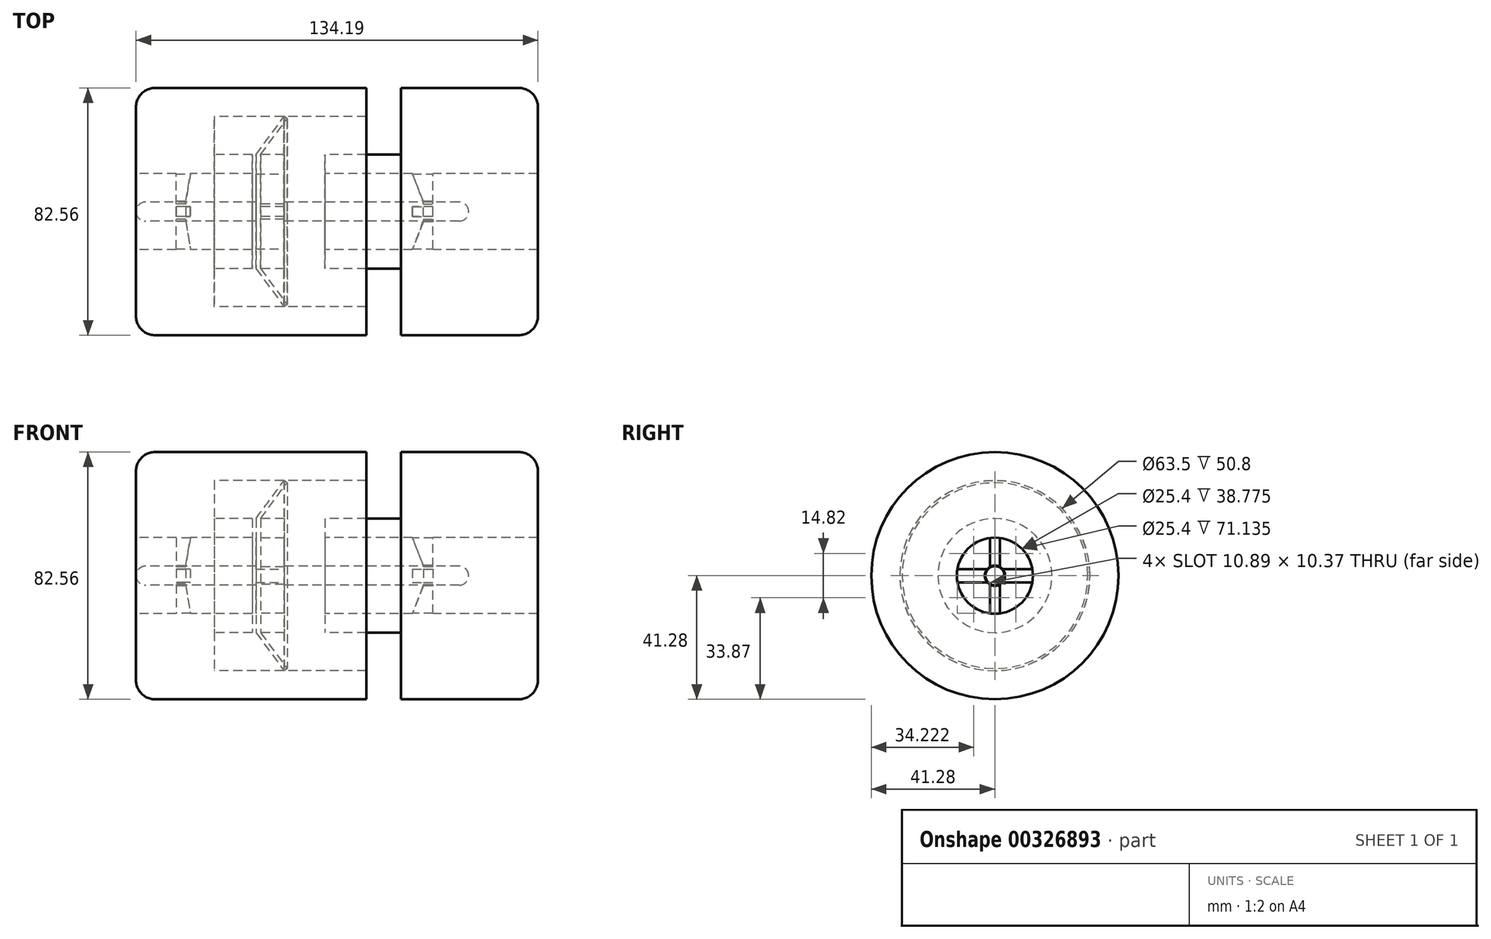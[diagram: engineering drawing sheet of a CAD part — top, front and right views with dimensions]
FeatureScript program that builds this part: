
annotation { "Feature Type Name" : "Feature", "Feature Type Description" : "" }
export const myFeature = defineFeature(function(context is Context, id is Id, definition is map)
    precondition{}
    {
        {
            var Q0;
            Q0=qCreatedBy(makeId("Front.planeOp"),FACE);
            var sketch = newSketch(context, id + "F0", { "sketchPlane" : qUnion([Q0])});
            skLineSegment(sketch, "E0", {"start": v(-134.2, 0) * mm, "end": v(170.75, 0) * mm, "construction": true});
            skLineSegment(sketch, "E1", {"start": v(-116.04, 12.7) * mm, "end": v(-95.42, 12.7) * mm});
            skLineSegment(sketch, "E2", {"start": v(-95.42, 12.7) * mm, "end": v(-95.42, 19.05) * mm});
            skLineSegment(sketch, "E3", {"start": v(-95.42, 19.05) * mm, "end": v(-108.12, 19.05) * mm});
            skLineSegment(sketch, "E4", {"start": v(-108.12, 19.05) * mm, "end": v(-108.12, 31.75) * mm});
            skLineSegment(sketch, "E5", {"start": v(-108.12, 31.75) * mm, "end": v(-57.32, 31.75) * mm});
            skLineSegment(sketch, "E6", {"start": v(-57.32, 31.75) * mm, "end": v(-57.32, 41.28) * mm});
            skLineSegment(sketch, "E7", {"start": v(-57.32, 41.28) * mm, "end": v(-127.84, 41.28) * mm});
            skLineSegment(sketch, "E8", {"start": v(-134.2, 34.93) * mm, "end": v(-134.2, 12.7) * mm});
            skLineSegment(sketch, "E9", {"start": v(-71.14, 12.7) * mm, "end": v(-45.74, 12.7) * mm});
            skLineSegment(sketch, "E10", {"start": v(-45.74, 19.05) * mm, "end": v(-45.74, 41.28) * mm});
            skLineSegment(sketch, "E11", {"start": v(-45.74, 41.28) * mm, "end": v(-6.35, 41.28) * mm});
            skLineSegment(sketch, "E12", {"start": v(0, 12.7) * mm, "end": v(-35.07, 12.7) * mm});
            skLineSegment(sketch, "E13", {"start": v(-71.14, 12.7) * mm, "end": v(-71.14, 19.05) * mm});
            skLineSegment(sketch, "E14", {"start": v(-71.14, 19.05) * mm, "end": v(-45.74, 19.05) * mm});
            skLineSegment(sketch, "E15", {"start": v(-120.82, 12.7) * mm, "end": v(-134.2, 12.7) * mm});
            skLineSegment(sketch, "E16", {"start": v(0, 12.7) * mm, "end": v(0, 34.93) * mm});
            skPoint(sketch, "E17.end.orphan", {"position": v(81.26, 12.7) * mm});
            skPoint(sketch, "E18.visualSharp", {"position": v(-134.2, 41.28) * mm});
            skArc(sketch, "E18.filletArc", {"start": v(-127.84, 41.28) * mm, "mid": v(-132.33, 39.42) * mm, "end": v(-134.2, 34.93) * mm});
            skPoint(sketch, "E19.visualSharp", {"position": v(0, 41.28) * mm});
            skArc(sketch, "E19.filletArc", {"start": v(0, 34.93) * mm, "mid": v(-1.86, 39.42) * mm, "end": v(-6.35, 41.27) * mm});
            skLineSegment(sketch, "E20", {"start": v(-94.15, 3.17) * mm, "end": v(-94.15, 19.05) * mm});
            skLineSegment(sketch, "E21", {"start": v(-94.15, 19.05) * mm, "end": v(-84.77, 31.72) * mm});
            skLineSegment(sketch, "E22", {"start": v(-84.7, 31.72) * mm, "end": v(-83.75, 31.01) * mm});
            skLineSegment(sketch, "E23", {"start": v(-83.75, 31.01) * mm, "end": v(-92.6, 19.05) * mm});
            skLineSegment(sketch, "E24", {"start": v(-92.6, 19.05) * mm, "end": v(-84.75, 19.05) * mm});
            skLineSegment(sketch, "E25", {"start": v(-84.75, 19.05) * mm, "end": v(-84.75, 3.17) * mm});
            skLineSegment(sketch, "E26", {"start": v(-84.75, 0) * mm, "end": v(-94.15, 0) * mm});
            skLineSegment(sketch, "E27", {"start": v(-94.15, 3.17) * mm, "end": v(-131.02, 3.17) * mm});
            skLineSegment(sketch, "E28", {"start": v(-26.3, 3.17) * mm, "end": v(-94.15, 3.17) * mm});
            skLineSegment(sketch, "E29", {"start": v(-23.12, 0) * mm, "end": v(-134.2, 0) * mm});
            skLineSegment(sketch, "E30", {"start": v(-120.82, 12.7) * mm, "end": v(-120.82, 3.37) * mm});
            skLineSegment(sketch, "E31", {"start": v(-120.82, 3.37) * mm, "end": v(-117.64, 3.37) * mm});
            skLineSegment(sketch, "E32", {"start": v(-117.64, 3.37) * mm, "end": v(-116.04, 12.7) * mm});
            skLineSegment(sketch, "E33", {"start": v(-35.07, 12.7) * mm, "end": v(-35.07, 3.39) * mm});
            skLineSegment(sketch, "E34", {"start": v(-35.07, 3.39) * mm, "end": v(-38.25, 3.39) * mm});
            skLineSegment(sketch, "E35", {"start": v(-38.25, 3.39) * mm, "end": v(-41.9, 12.7) * mm});
            skLineSegment(sketch, "E36.trimOffspring", {"start": v(-41.9, 12.7) * mm, "end": v(-45.74, 12.7) * mm});
            skLineSegment(sketch, "E37", {"start": v(-84.77, 31.72) * mm, "end": v(-84.7, 31.72) * mm});
            skPoint(sketch, "E38.orphan", {"position": v(-84.75, 31.75) * mm});
            skLineSegment(sketch, "E39", {"start": v(-134.2, 0) * mm, "end": v(-131.02, 0) * mm});
            skLineSegment(sketch, "E40", {"start": v(-23.12, 0) * mm, "end": v(-26.3, 0) * mm});
            skArc(sketch, "E41", {"start": v(-23.12, 0) * mm, "mid": v(-24.05, 2.25) * mm, "end": v(-26.3, 3.18) * mm});
            skArc(sketch, "E42", {"start": v(-134.2, 0) * mm, "mid": v(-133.26, 2.25) * mm, "end": v(-131.02, 3.18) * mm});
            skPoint(sketch, "E43.start.orphan", {"position": v(-134.2, 3.17) * mm});
            skPoint(sketch, "E44.end.orphan", {"position": v(-23.12, 3.18) * mm});
            skSolve(sketch);
        }
        {
            var Q0;
            Q0 = qSketchRegion(id + "F0", true);
            var Q1;
            Q1=sQuery(id+"F0.wireOp",EDGE,"E0");
            revolve(context, id + "F1", {"entities" : qUnion([Q0]), "axis" : qUnion([Q1]), "revolveType" : RevolveType.FULL});
        }
        {
            var Q0;
            Q0=makeQuery(id+"F1.opRevolve","SWEPT_FACE",FACE,{"disambiguationData":[OSD([sQuery(id+"F0.wireOp",EDGE,"E33")])]});
            var sketch = newSketch(context, id + "F2", { "sketchPlane" : qUnion([Q0])});
            skLineSegment(sketch, "E45.bottom", {"start": v(2.22, 14) * mm, "end": v(-2.22, 14) * mm});
            skLineSegment(sketch, "E45.top", {"start": v(2.22, -14) * mm, "end": v(-2.22, -14) * mm});
            skLineSegment(sketch, "E45.left", {"start": v(2.22, 14) * mm, "end": v(2.22, -14) * mm});
            skLineSegment(sketch, "E45.right", {"start": v(-2.22, 14) * mm, "end": v(-2.22, -14) * mm});
            skPoint(sketch, "E45.middle", {"position": v(0, 0) * mm});
            skLineSegment(sketch, "E46.bottom", {"start": v(-13.97, 2.22) * mm, "end": v(13.97, 2.22) * mm});
            skLineSegment(sketch, "E46.top", {"start": v(-13.97, -2.22) * mm, "end": v(13.97, -2.22) * mm});
            skLineSegment(sketch, "E46.left", {"start": v(-13.97, 2.22) * mm, "end": v(-13.97, -2.22) * mm});
            skLineSegment(sketch, "E46.right", {"start": v(13.97, 2.22) * mm, "end": v(13.97, -2.22) * mm});
            skSolve(sketch);
        }
        {
            var Q0;
            {var subQ0=sQuery(id+"F2.wireOp",EDGE,"E45.right");var subQ1=sQuery(id+"F0.wireOp",EDGE,"E33");var subQ2=makeQuery(id+"F1.opRevolve","SWEPT_EDGE",EDGE,{"disambiguationData":[OSD([sQuery(id+"F0.wireOp",EDGE,"E12"),subQ1])]});var subQ3=makeQuery(id+"F2.imprint","INTERSECT",VERTEX,{"disambiguationData":[OD(0.0)],"derivedFrom":[subQ2,subQ0]});Q0=makeQuery(id+"F2.imprint","IMPRINT",FACE,{"disambiguationData":[TD([[makeQuery(id+"F2.imprint","IMPRINT",EDGE,{"disambiguationData":[TD([[subQ3,-1.0]])],"derivedFrom":subQ0}),-1.0]])]});}
            var Q1;
            {var subQ0=sQuery(id+"F2.wireOp",EDGE,"E45.right");var subQ1=sQuery(id+"F0.wireOp",EDGE,"E33");var subQ2=makeQuery(id+"F1.opRevolve","SWEPT_EDGE",EDGE,{"disambiguationData":[OSD([sQuery(id+"F0.wireOp",EDGE,"E12"),subQ1])]});var subQ3=makeQuery(id+"F2.imprint","INTERSECT",VERTEX,{"disambiguationData":[OD(1.0)],"derivedFrom":[subQ2,subQ0]});Q1=makeQuery(id+"F2.imprint","IMPRINT",FACE,{"disambiguationData":[TD([[makeQuery(id+"F2.imprint","IMPRINT",EDGE,{"disambiguationData":[TD([[subQ3,1.0]])],"derivedFrom":subQ0}),-1.0]])]});}
            var Q2;
            {var subQ0=sQuery(id+"F2.wireOp",EDGE,"E45.left");var subQ1=sQuery(id+"F0.wireOp",EDGE,"E33");var subQ2=makeQuery(id+"F1.opRevolve","SWEPT_EDGE",EDGE,{"disambiguationData":[OSD([sQuery(id+"F0.wireOp",EDGE,"E12"),subQ1])]});var subQ3=makeQuery(id+"F2.imprint","INTERSECT",VERTEX,{"disambiguationData":[OD(1.0)],"derivedFrom":[subQ2,subQ0]});Q2=makeQuery(id+"F2.imprint","IMPRINT",FACE,{"disambiguationData":[TD([[makeQuery(id+"F2.imprint","IMPRINT",EDGE,{"disambiguationData":[TD([[subQ3,1.0]])],"derivedFrom":subQ0}),1.0]])]});}
            var Q3;
            {var subQ0=sQuery(id+"F2.wireOp",EDGE,"E45.left");var subQ1=sQuery(id+"F0.wireOp",EDGE,"E33");var subQ2=makeQuery(id+"F1.opRevolve","SWEPT_EDGE",EDGE,{"disambiguationData":[OSD([sQuery(id+"F0.wireOp",EDGE,"E12"),subQ1])]});var subQ3=makeQuery(id+"F2.imprint","INTERSECT",VERTEX,{"disambiguationData":[OD(0.0)],"derivedFrom":[subQ2,subQ0]});Q3=makeQuery(id+"F2.imprint","IMPRINT",FACE,{"disambiguationData":[TD([[makeQuery(id+"F2.imprint","IMPRINT",EDGE,{"disambiguationData":[TD([[subQ3,-1.0]])],"derivedFrom":subQ0}),1.0]])]});}
            extrude(context, id + "F3", {"entities" : qUnion([Q0, Q1, Q2, Q3]), "operationType" : NewBodyOperationType.REMOVE, "endBound" : BoundingType.THROUGH_ALL, "oppositeDirection" : true, "depth" : 25.4 * mm});
        }
        {
            var Q0;
            Q0=makeQuery(id+"F1.opRevolve","SWEPT_FACE",FACE,{"disambiguationData":[OSD([sQuery(id+"F0.wireOp",EDGE,"E30")])]});
            var sketch = newSketch(context, id + "F4", { "sketchPlane" : qUnion([Q0])});
            skLineSegment(sketch, "E47.bottom", {"start": v(1.61, 15.52) * mm, "end": v(-1.61, 15.52) * mm});
            skLineSegment(sketch, "E47.top", {"start": v(1.61, -15.52) * mm, "end": v(-1.61, -15.52) * mm});
            skLineSegment(sketch, "E47.left", {"start": v(1.61, 15.52) * mm, "end": v(1.61, -15.52) * mm});
            skLineSegment(sketch, "E47.right", {"start": v(-1.61, 15.52) * mm, "end": v(-1.61, -15.52) * mm});
            skPoint(sketch, "E47.middle", {"position": v(0, 0) * mm});
            skLineSegment(sketch, "E48.bottom", {"start": v(-19.05, 2.22) * mm, "end": v(19.05, 2.22) * mm});
            skLineSegment(sketch, "E48.top", {"start": v(-19.05, -2.22) * mm, "end": v(19.05, -2.22) * mm});
            skLineSegment(sketch, "E48.left", {"start": v(-19.05, 2.22) * mm, "end": v(-19.05, -2.22) * mm});
            skLineSegment(sketch, "E48.right", {"start": v(19.05, 2.22) * mm, "end": v(19.05, -2.22) * mm});
            skSolve(sketch);
        }
        {
            var Q0;
            {var subQ0=sQuery(id+"F4.wireOp",EDGE,"E47.right");var subQ1=sQuery(id+"F0.wireOp",EDGE,"E30");var subQ2=makeQuery(id+"F1.opRevolve","SWEPT_EDGE",EDGE,{"disambiguationData":[OSD([sQuery(id+"F0.wireOp",EDGE,"E15"),subQ1])]});var subQ3=makeQuery(id+"F4.imprint","INTERSECT",VERTEX,{"disambiguationData":[OD(0.0)],"derivedFrom":[subQ2,subQ0]});Q0=makeQuery(id+"F4.imprint","IMPRINT",FACE,{"disambiguationData":[TD([[makeQuery(id+"F4.imprint","IMPRINT",EDGE,{"disambiguationData":[TD([[subQ3,-1.0]])],"derivedFrom":subQ0}),-1.0]])]});}
            var Q1;
            {var subQ0=sQuery(id+"F4.wireOp",EDGE,"E47.left");var subQ1=sQuery(id+"F0.wireOp",EDGE,"E30");var subQ2=makeQuery(id+"F1.opRevolve","SWEPT_EDGE",EDGE,{"disambiguationData":[OSD([sQuery(id+"F0.wireOp",EDGE,"E15"),subQ1])]});var subQ3=makeQuery(id+"F4.imprint","INTERSECT",VERTEX,{"disambiguationData":[OD(0.0)],"derivedFrom":[subQ2,subQ0]});Q1=makeQuery(id+"F4.imprint","IMPRINT",FACE,{"disambiguationData":[TD([[makeQuery(id+"F4.imprint","IMPRINT",EDGE,{"disambiguationData":[TD([[subQ3,-1.0]])],"derivedFrom":subQ0}),1.0]])]});}
            var Q2;
            {var subQ0=sQuery(id+"F4.wireOp",EDGE,"E47.left");var subQ1=sQuery(id+"F0.wireOp",EDGE,"E30");var subQ2=makeQuery(id+"F1.opRevolve","SWEPT_EDGE",EDGE,{"disambiguationData":[OSD([sQuery(id+"F0.wireOp",EDGE,"E15"),subQ1])]});var subQ3=makeQuery(id+"F4.imprint","INTERSECT",VERTEX,{"disambiguationData":[OD(1.0)],"derivedFrom":[subQ2,subQ0]});Q2=makeQuery(id+"F4.imprint","IMPRINT",FACE,{"disambiguationData":[TD([[makeQuery(id+"F4.imprint","IMPRINT",EDGE,{"disambiguationData":[TD([[subQ3,1.0]])],"derivedFrom":subQ0}),1.0]])]});}
            var Q3;
            {var subQ0=sQuery(id+"F4.wireOp",EDGE,"E47.right");var subQ1=sQuery(id+"F0.wireOp",EDGE,"E30");var subQ2=makeQuery(id+"F1.opRevolve","SWEPT_EDGE",EDGE,{"disambiguationData":[OSD([sQuery(id+"F0.wireOp",EDGE,"E15"),subQ1])]});var subQ3=makeQuery(id+"F4.imprint","INTERSECT",VERTEX,{"disambiguationData":[OD(1.0)],"derivedFrom":[subQ2,subQ0]});Q3=makeQuery(id+"F4.imprint","IMPRINT",FACE,{"disambiguationData":[TD([[makeQuery(id+"F4.imprint","IMPRINT",EDGE,{"disambiguationData":[TD([[subQ3,1.0]])],"derivedFrom":subQ0}),-1.0]])]});}
            extrude(context, id + "F5", {"entities" : qUnion([Q0, Q1, Q2, Q3]), "operationType" : NewBodyOperationType.REMOVE, "endBound" : BoundingType.THROUGH_ALL, "oppositeDirection" : true, "depth" : 25.4 * mm});
        }
    });
